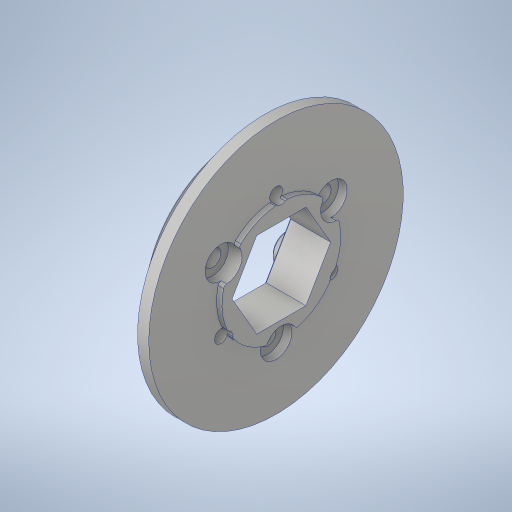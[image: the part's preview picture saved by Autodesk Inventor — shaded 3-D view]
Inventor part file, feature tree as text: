
AUTODESK INVENTOR PART (.ipt)
format: ipt  version: 2023.4 (Build 274418000, 418)  size: 519,168 bytes
history: native  units: in
note: dims shown in document units (in); Inventor stores cm internally (conversion verified against a paired STEP export)
features: chamfer x1
ambient origin geometry x8: Origin, YZ Plane, XZ Plane, XY Plane, X Axis, Y Axis, Z Axis, Center Point
bodies: Solid1 (feature_tree)
feature tree (1):
  chamfer  "Chamfer2"  [1 undecoded]
note: 1 required parameter value undecoded (feature->parameter linkage not recoverable at this tier; creation-order binding heuristic only, values carry confidence <= 0.55)
